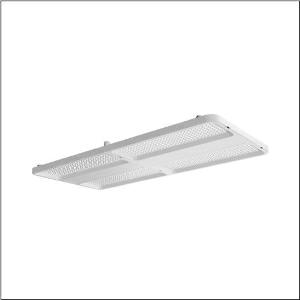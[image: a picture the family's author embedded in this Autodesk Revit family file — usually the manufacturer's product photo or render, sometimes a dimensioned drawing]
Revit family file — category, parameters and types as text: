
# Revit family: highbay_21_maxi_52hn12db5qda
name_source: partatom
category: Lighting Fixtures
units: mm (PartAtom-declared; Revit-internal decimal feet)

## family parameters
Cut with Voids When Loaded = No
Host = Face
Light Source = No
Part Type = Normal
Room Calculation Point = No
Round Connector Dimension = Use Diameter
Shared = No

## types (1)
- --- (1 x LED, 5680 lm, 31.4 W, 5000K)
    Apparent Load = 31 VA
    CIE Flux Codes = 90 98 100 100 100
    Color Rendering = 80
    Color Temperature = 5000K
    Default Elevation = 1800 mm
    Description = high bay luminaire Highbay 21 maxi; direct symmetric wide distribution, light control with lens of PMMA; UGR ≤ 22 (X = 4H | Y = 8H | S = 0.25H | reflection values 70/50/20); luminous flux: 36.980lm; light colour: 850, colour temperature: 5000K, MacAdam ≤ 3 SDCM (initial), colour rendering: CRI > 80; luminous efficacy: 187,1lm/W; rated service life: 75.000h (L80) at AT= ta max; control: DALI 2; luminaire connection: terminal, 5-pole, max. 2.5mm² (cable entry for one cable, Ø 8.5..16mm); mains connection: 230..240V, AC/DC 0/50..60Hz; connected load: 197,7W; protection rating (complete): IP66; insulation class (complete): insulation class I (protective earthing); protection symbol: D; impact resistance: IK08; certification: CE, ENEC, VDE, UKCA; luminaire for central battery installations according to EN 60598-2-22, internal wiring halogen-free; luminaire LABS conformity tested according to VDMA 24364:2018-05; Suitable for use in the food industry according to the specifications of IFS-Food, HACCP and/or BRC; housing frame of high-performance plastic PA6, matt traffic white (RAL 9016); cover of PMMA; dimension (LxWxH): 946 x 442 x 72mm; permissible operating ambient temperature: -40..+60°C (reducing of maximum allowable ambient temperature of 5°C with ceiling mounting); packaging unit: 1 piece; (delivery without accessories; please order mounting accessories separately)
    Height = 72 mm  [stored 0.23622 ft]
    Lamp = 1 x LED
    Lamp Light Flux = 5680 lm
    Lamp Power = 31.4 W
    Lamp count = 1
    Length = 946 mm
    Luminous efficacy = 181 lm/W
    Manufacturer = Siteco
    ModVariant = No
    Model = 52HN12DB5QDA
    Mounting Place = Ceiling
    Mounting Type = Pendant
    Number of Poles = 1
    OnlyDefault = Yes
    Power Factor = 1
    Product Name = Highbay 21 maxi
    Product group = high bay luminaire
    ProductGroupID = 902
    Protection Class = Protection class I
    Protection Degree = IP 66
    RLX_Detail_Level = 1
    RLX_Emergency_Light_Flux = 0 lm
    RLX_Emergency_Type = 0
    RLX_Emergency_Type_DB = No
    RlxData = <blob elided: 128253 chars, md5=af44ff51>
    Socket = socket
    Standby Power = 0 W
    System Light Flux = 5680 lm
    System Power = 31 W
    Type Comments = : DC mode (central or group accumulator) initial emergency light level
    Type Image = l_1363244.jpg
    URL = http://relux.com
    VarID = @adj_004883
    Voltage = 0 V
    Weight = 0.00 kg
    Width = 442 mm

note: [stored X ft] marks values corroborated as IEEE doubles in the binary element streams (Revit-internal decimal feet)

## geometry (parser evidence)
native form markers: Blend x4, Sweep x9
no freeform markers — native parametric forms only
